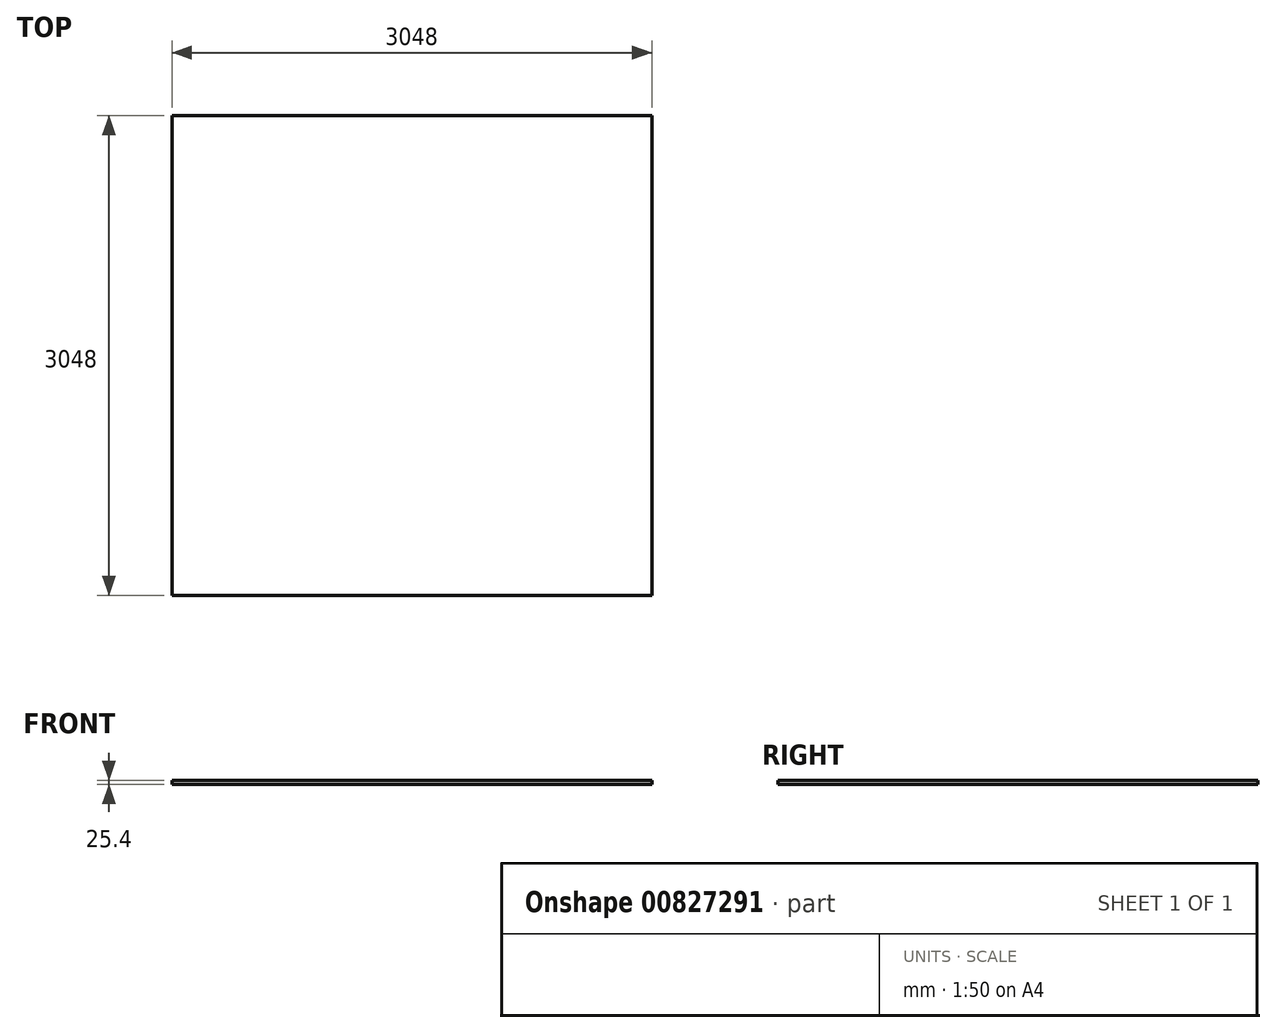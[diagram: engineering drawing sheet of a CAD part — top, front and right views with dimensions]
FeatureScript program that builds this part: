
annotation { "Feature Type Name" : "Feature", "Feature Type Description" : "" }
export const myFeature = defineFeature(function(context is Context, id is Id, definition is map)
    precondition{}
    {
        {
            var Q0;
            Q0=qCreatedBy(makeId("Top.planeOp"),FACE);
            var sketch = newSketch(context, id + "F0", { "sketchPlane" : qUnion([Q0])});
            skLineSegment(sketch, "E0.bottom", {"start": v(0, 0) * mm, "end": v(3048, 0) * mm});
            skLineSegment(sketch, "E0.top", {"start": v(0, 3048) * mm, "end": v(3048, 3048) * mm});
            skLineSegment(sketch, "E0.left", {"start": v(0, 0) * mm, "end": v(0, 3048) * mm});
            skLineSegment(sketch, "E0.right", {"start": v(3048, 0) * mm, "end": v(3048, 3048) * mm});
            skSolve(sketch);
        }
        {
            var Q0;
            Q0=qSketchRegion(id+"F0",true);
            extrude(context, id + "F1", {"entities" : qUnion([Q0]), "depth" : 25.4 * mm});
        }
    });
